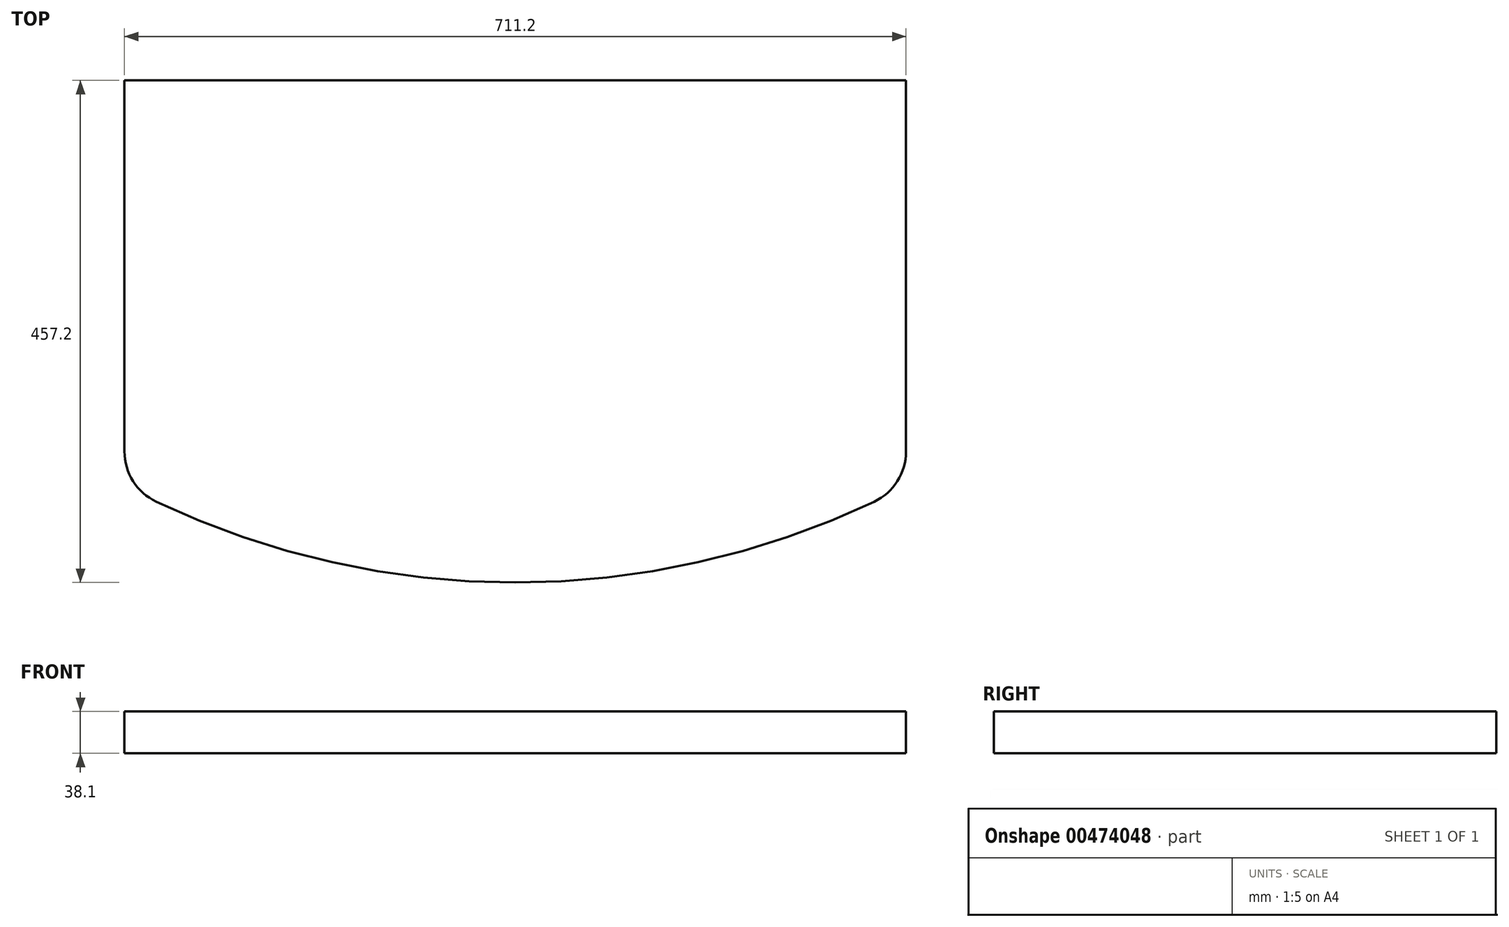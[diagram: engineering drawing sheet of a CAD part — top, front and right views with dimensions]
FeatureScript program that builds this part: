
annotation { "Feature Type Name" : "Feature", "Feature Type Description" : "" }
export const myFeature = defineFeature(function(context is Context, id is Id, definition is map)
    precondition{}
    {
        {
            var Q0;
            Q0=qCreatedBy(makeId("Top.planeOp"),FACE);
            var sketch = newSketch(context, id + "F0", { "sketchPlane" : qUnion([Q0])});
            skLineSegment(sketch, "E0.bottom", {"start": v(558.8, 0) * mm, "end": v(1270, 0) * mm});
            skArc(sketch, "E1", {"start": v(587.83, -383.67) * mm, "mid": v(914.4, -457.2) * mm, "end": v(1240.97, -383.67) * mm});
            skLineSegment(sketch, "E2", {"start": v(558.8, 0) * mm, "end": v(558.8, -337.77) * mm});
            skLineSegment(sketch, "E3", {"start": v(1270, 0) * mm, "end": v(1270, -337.77) * mm});
            skArc(sketch, "E4.filletArc", {"start": v(1240.97, -383.67) * mm, "mid": v(1262.13, -364.93) * mm, "end": v(1270, -337.77) * mm});
            skArc(sketch, "E5.filletArc", {"start": v(558.8, -337.77) * mm, "mid": v(566.67, -364.93) * mm, "end": v(587.83, -383.67) * mm});
            skSolve(sketch);
        }
        {
            var Q0;
            Q0=makeQuery(id+"F0.imprint","IMPRINT",FACE,{"disambiguationData":[TD([[makeQuery(id+"F0.imprint","IMPRINT",EDGE,{"derivedFrom":sQuery(id+"F0.wireOp",EDGE,"E0.bottom")}),-1.0]])]});
            extrude(context, id + "F1", {"entities" : qUnion([Q0]), "endBound" : BoundingType.SYMMETRIC, "depth" : 38.1 * mm});
        }
    });
